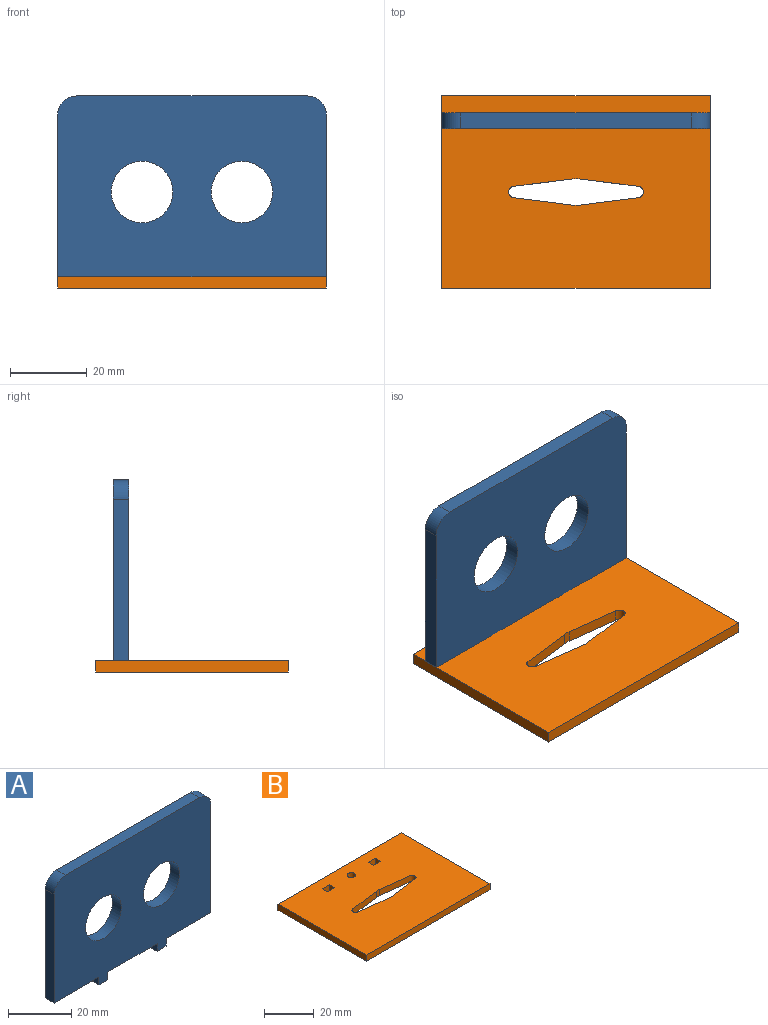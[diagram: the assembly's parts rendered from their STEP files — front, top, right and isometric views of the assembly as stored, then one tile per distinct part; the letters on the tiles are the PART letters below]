
ASSEMBLY  parts=2 mates=1
PART A: 18 faces, bbox 70x4x50 mm
  f0: plane 4x4mm, normal (0,0,-1), area 16mm2, adj f1,f15,f16,f17
  f1: plane 4x3mm, normal (1,0,0), area 12mm2, adj f0,f2,f16,f17
  f2: plane 20x4mm, normal (0,0,-1), area 80mm2, adj f1,f3,f16,f17
  f3: plane 42x4mm, normal (1,0,0), area 168mm2, adj f2,f4,f16,f17
  f4: cylinder r=5mm len=5mm, axis (0,1,0), area 31.4mm2, adj f3,f5,f16,f17
  f5: plane 60x4mm, normal (0,0,1), area 240mm2, adj f4,f6,f16,f17
  f6: cylinder r=5mm len=5mm, axis (0,1,0), area 31.4mm2, adj f5,f7,f16,f17
  f7: plane 42x4mm, normal (-1,0,0), area 168mm2, adj f6,f8,f16,f17
  f8: plane 20x4mm, normal (0,0,-1), area 80mm2, adj f7,f9,f16,f17
  f9: plane 4x3mm, normal (-1,0,0), area 12mm2, adj f8,f10,f16,f17
  f10: plane 4x4mm, normal (0,0,-1), area 16mm2, adj f9,f11,f16,f17
  f11: plane 4x3mm, normal (1,0,0), area 12mm2, adj f10,f12,f16,f17
  f12: plane 22x4mm, normal (0,0,-1), area 88mm2, adj f11,f15,f16,f17
  f13: cylinder r=8mm len=16mm, axis (0,1,0), area 201.1mm2, adj f16,f17
  f14: cylinder r=8mm len=16mm, axis (0,1,0), area 201.1mm2, adj f16,f17
  f15: plane 4x3mm, normal (-1,0,0), area 12mm2, adj f0,f12,f16,f17
  f16: plane 70x50mm, normal (0,-1,0), area 2901.1mm2, adj f0,f1,f2,f3,f4,f5,f6,f7
  f17: plane 70x50mm, normal (0,1,0), area 2901.1mm2, adj f0,f1,f2,f3,f4,f5,f6,f7
PART B: 22 faces, bbox 70x50x3 mm
  f0: plane 50x3mm, normal (-1,0,0), area 150mm2, adj f1,f19,f20,f21
  f1: plane 70x3mm, normal (0,-1,0), area 210mm2, adj f0,f2,f20,f21
  f2: plane 50x3mm, normal (1,0,0), area 150mm2, adj f1,f19,f20,f21
  f3: plane 4x3mm, normal (0,1,0), area 12mm2, adj f4,f15,f20,f21
  f4: plane 3x3mm, normal (1,0,0), area 9mm2, adj f3,f5,f20,f21
  f5: plane 4x3mm, normal (0,-1,0), area 12mm2, adj f4,f15,f20,f21
  f6: plane 4x3mm, normal (0,-1,0), area 12mm2, adj f7,f16,f20,f21
  f7: plane 3x3mm, normal (-1,0,0), area 9mm2, adj f6,f8,f20,f21
  f8: plane 4x3mm, normal (0,1,0), area 12mm2, adj f7,f16,f20,f21
  f9: cylinder r=3.5mm len=3mm, axis (0,0,-1), area 5.2mm2, adj f10,f17,f20,f21
  f10: plane 15.33x3mm, normal (-0.12,-0.99,0), area 46.3mm2, adj f9,f11,f20,f21
  f11: cylinder r=1.5mm len=3mm, axis (0,0,-1), area 13.5mm2, adj f10,f12,f20,f21
  f12: plane 16.01x3mm, normal (-0.13,0.99,0), area 48.4mm2, adj f11,f13,f20,f21
  f13: plane 16.01x3mm, normal (0.13,0.99,0), area 48.4mm2, adj f12,f14,f20,f21
  f14: cylinder r=1.5mm len=3mm, axis (0,0,-1), area 13.5mm2, adj f13,f17,f20,f21
  f15: plane 3x3mm, normal (-1,0,0), area 9mm2, adj f3,f5,f20,f21
  f16: plane 3x3mm, normal (1,0,0), area 9mm2, adj f6,f8,f20,f21
  f17: plane 15.33x3mm, normal (0.12,-0.99,0), area 46.3mm2, adj f9,f14,f20,f21
  f18: cylinder r=1.67mm len=3.34mm, axis (0,0,-1), area 31.5mm2, adj f20,f21
  f19: plane 70x3mm, normal (0,1,0), area 210mm2, adj f0,f2,f20,f21
  f20: plane 70x50mm, normal (0,0,1), area 3299.5mm2, adj f0,f1,f2,f3,f4,f5,f6,f7
  f21: plane 70x50mm, normal (0,0,-1), area 3299.5mm2, adj f0,f1,f2,f3,f4,f5,f6,f7
PLACE A t=(-41.8,-0.33,4.33)mm
PLACE B t=(-41.8,-20.83,-20.67)mm
MATE fastened A.f1 <-> B.f15  axis (1,0,0) through (-26.8,-2.33,-19.17)mm
